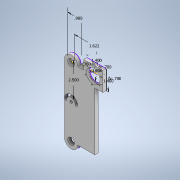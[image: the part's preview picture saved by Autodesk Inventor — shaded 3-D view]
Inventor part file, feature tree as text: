
AUTODESK INVENTOR PART (.ipt)
format: ipt  version: 2021 (Build 250183000, 183)  size: 178,688 bytes
history: native  units: in
note: dims shown in document units (in); Inventor stores cm internally (conversion verified against a paired STEP export)
features: extrude x5, sketch x4, hole x3, projected_geometry x2
ambient origin geometry x8: Origin, YZ Plane, XZ Plane, XY Plane, X Axis, Y Axis, Z Axis, Center Point
bodies: Solid1 (feature_tree)
feature tree (14):
  extrude  "Extrusion1"  Depth=0.98in
  hole  "Hole1"  [1 undecoded]
  hole  "Hole2"  [1 undecoded]
  extrude  "Extrusion2"  TaperAngle=0.0deg  [1 undecoded]
  extrude  "Extrusion3"  Depth=1.4in TaperAngle=0.0deg
  sketch  "Sketch5"  dims[d11=0.2in d12=0.172in d13=0.375in d14=0.25in d15=0.5635in d16=0.2275in d17=0.8108in d18=0.08in d19=0.3937in d20=0.0in d21=0.0in d22=1.25in d23=0.0in d24=1.4in d25=1.4in d26=1.0in d27=0.7in d28=0.7in d29=0.6102in d30=2.3622in d32=360.0deg d34=1.25in d35=0.0in d36=0.0in d37=0.0in d38=0.092in d39=0.172in d40=0.375in d41=0.25in d42=0.5635in d43=0.2275in d44=0.8108in d45=1.6216in]
  extrude  "Extrusion4"  Depth=1.4in
  extrude  "Extrusion5"  Depth=1.4in
  hole  "Hole3"  [1 undecoded]
  sketch  "Sketch2"  dims[d0=2.5in d1=0.98in]
  projected_geometry  "Projected Loop1"
  sketch  "Sketch3"  dims[d2=0.24in d3=0.0in]
  sketch  "Sketch4"  dims[d4=0.49in d5=0.172in d6=0.375in d7=0.25in d8=0.5635in d9=0.2275in d10=0.8108in]
  projected_geometry  "Projected Loop2"
note: 4 required parameter values undecoded (feature->parameter linkage not recoverable at this tier; creation-order binding heuristic only, values carry confidence <= 0.55)
